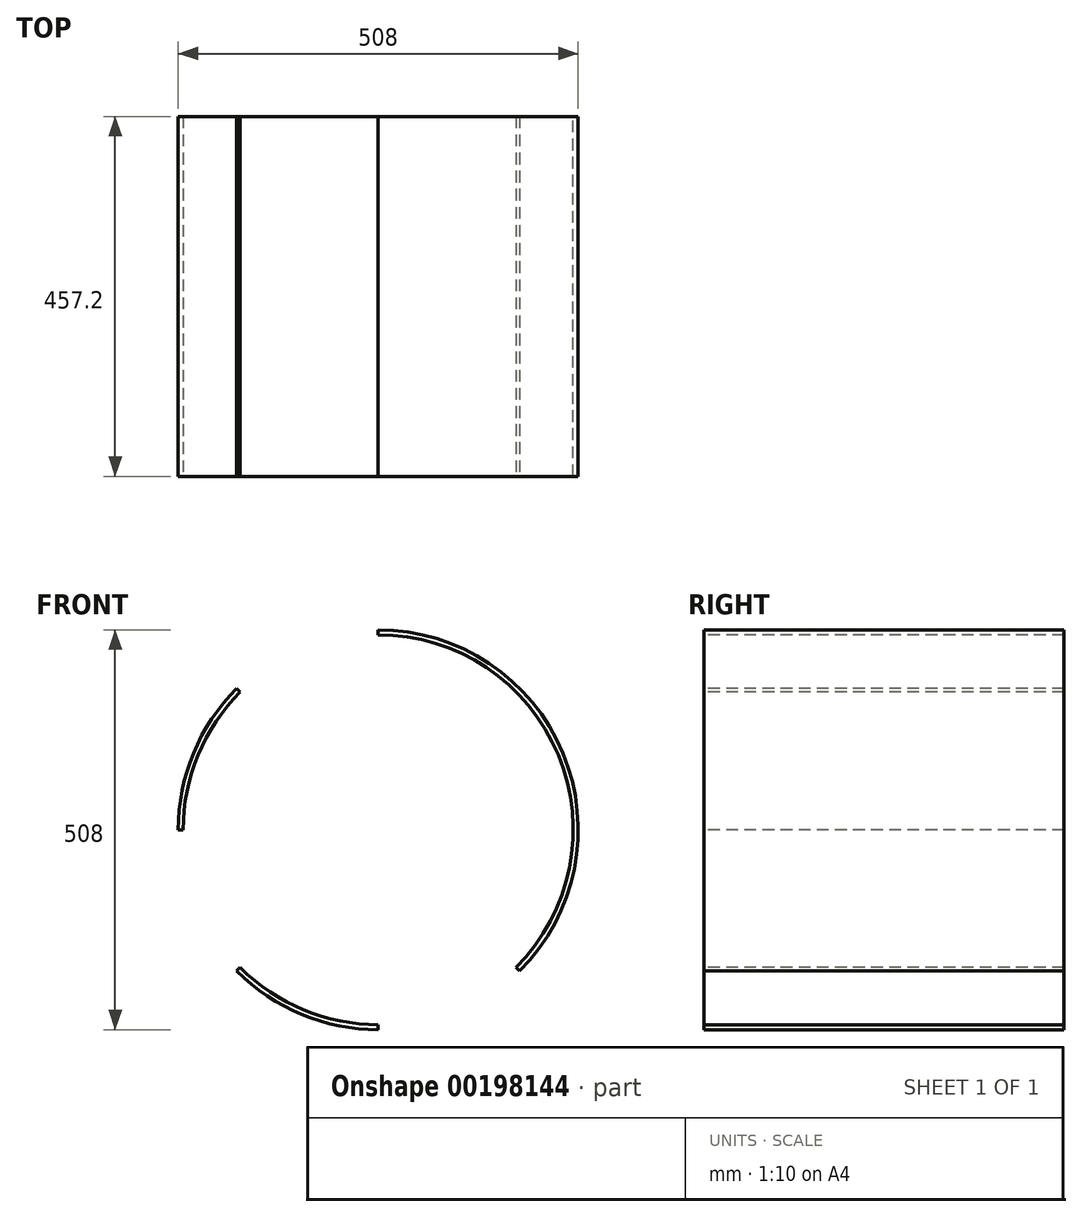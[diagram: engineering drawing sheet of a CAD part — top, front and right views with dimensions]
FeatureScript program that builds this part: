
annotation { "Feature Type Name" : "Feature", "Feature Type Description" : "" }
export const myFeature = defineFeature(function(context is Context, id is Id, definition is map)
    precondition{}
    {
        {
            var Q0;
            Q0=qCreatedBy(makeId("Front.planeOp"),FACE);
            var sketch = newSketch(context, id + "F0", { "sketchPlane" : qUnion([Q0])});
            skCircle(sketch, "E0", {"center": v(0, 0) * mm, "radius": 254 * mm});
            skCircle(sketch, "E1", {"center": v(0, 0) * mm, "radius": 247.65 * mm});
            skLineSegment(sketch, "E2", {"start": v(0, 355.76) * mm, "end": v(0, -339.23) * mm});
            skLineSegment(sketch, "E3", {"start": v(-324.34, 0) * mm, "end": v(365.41, 0) * mm});
            skLineSegment(sketch, "E4", {"start": v(253.63, 253.63) * mm, "end": v(-253.63, -253.63) * mm});
            skLineSegment(sketch, "E5", {"start": v(-285.77, 285.77) * mm, "end": v(285.77, -285.77) * mm});
            skSolve(sketch);
        }
        {
            var Q0;
            Q0 = qSketchRegion(id + "F0", true);
            extrude(context, id + "F1", {"entities" : qUnion([Q0]), "endBound" : BoundingType.SYMMETRIC, "depth" : 457.2 * mm});
        }
        {
            var Q0;
            {var subQ0=sQuery(id+"F0.wireOp",EDGE,"E2");var subQ1=sQuery(id+"F0.wireOp",EDGE,"E0");var subQ2=makeQuery(id+"F0.imprint","INTERSECT",VERTEX,{"disambiguationData":[OD(0.0)],"derivedFrom":[subQ1,subQ0]});Q0=makeQuery(id+"F0.imprint","IMPRINT",FACE,{"disambiguationData":[TD([[makeQuery(id+"F0.imprint","IMPRINT",EDGE,{"disambiguationData":[TD([[subQ2,-1.0]])],"derivedFrom":subQ1}),1.0]])]});}
            var Q1;
            {var subQ0=sQuery(id+"F0.wireOp",EDGE,"E3");var subQ1=sQuery(id+"F0.wireOp",EDGE,"E0");var subQ2=makeQuery(id+"F0.imprint","INTERSECT",VERTEX,{"disambiguationData":[OD(1.0)],"derivedFrom":[subQ1,subQ0]});Q1=makeQuery(id+"F0.imprint","IMPRINT",FACE,{"disambiguationData":[TD([[makeQuery(id+"F0.imprint","IMPRINT",EDGE,{"disambiguationData":[TD([[subQ2,-1.0]])],"derivedFrom":subQ1}),1.0]])]});}
            var Q2;
            {var subQ0=sQuery(id+"F0.wireOp",EDGE,"E2");var subQ1=sQuery(id+"F0.wireOp",EDGE,"E0");var subQ2=makeQuery(id+"F0.imprint","INTERSECT",VERTEX,{"disambiguationData":[OD(1.0)],"derivedFrom":[subQ1,subQ0]});Q2=makeQuery(id+"F0.imprint","IMPRINT",FACE,{"disambiguationData":[TD([[makeQuery(id+"F0.imprint","IMPRINT",EDGE,{"disambiguationData":[TD([[subQ2,-1.0]])],"derivedFrom":subQ1}),1.0]])]});}
            var Q3;
            {var subQ0=sQuery(id+"F0.wireOp",EDGE,"E4");var subQ1=sQuery(id+"F0.wireOp",EDGE,"E0");var subQ2=makeQuery(id+"F0.imprint","INTERSECT",VERTEX,{"disambiguationData":[OD(0.0)],"derivedFrom":[subQ1,subQ0]});Q3=makeQuery(id+"F0.imprint","IMPRINT",FACE,{"disambiguationData":[TD([[makeQuery(id+"F0.imprint","IMPRINT",EDGE,{"disambiguationData":[TD([[subQ2,1.0]])],"derivedFrom":subQ1}),1.0]])]});}
            extrude(context, id + "F2", {"entities" : qUnion([Q0, Q1, Q2, Q3]), "operationType" : NewBodyOperationType.REMOVE, "endBound" : BoundingType.SYMMETRIC, "oppositeDirection" : true, "depth" : 508 * mm});
        }
    });
